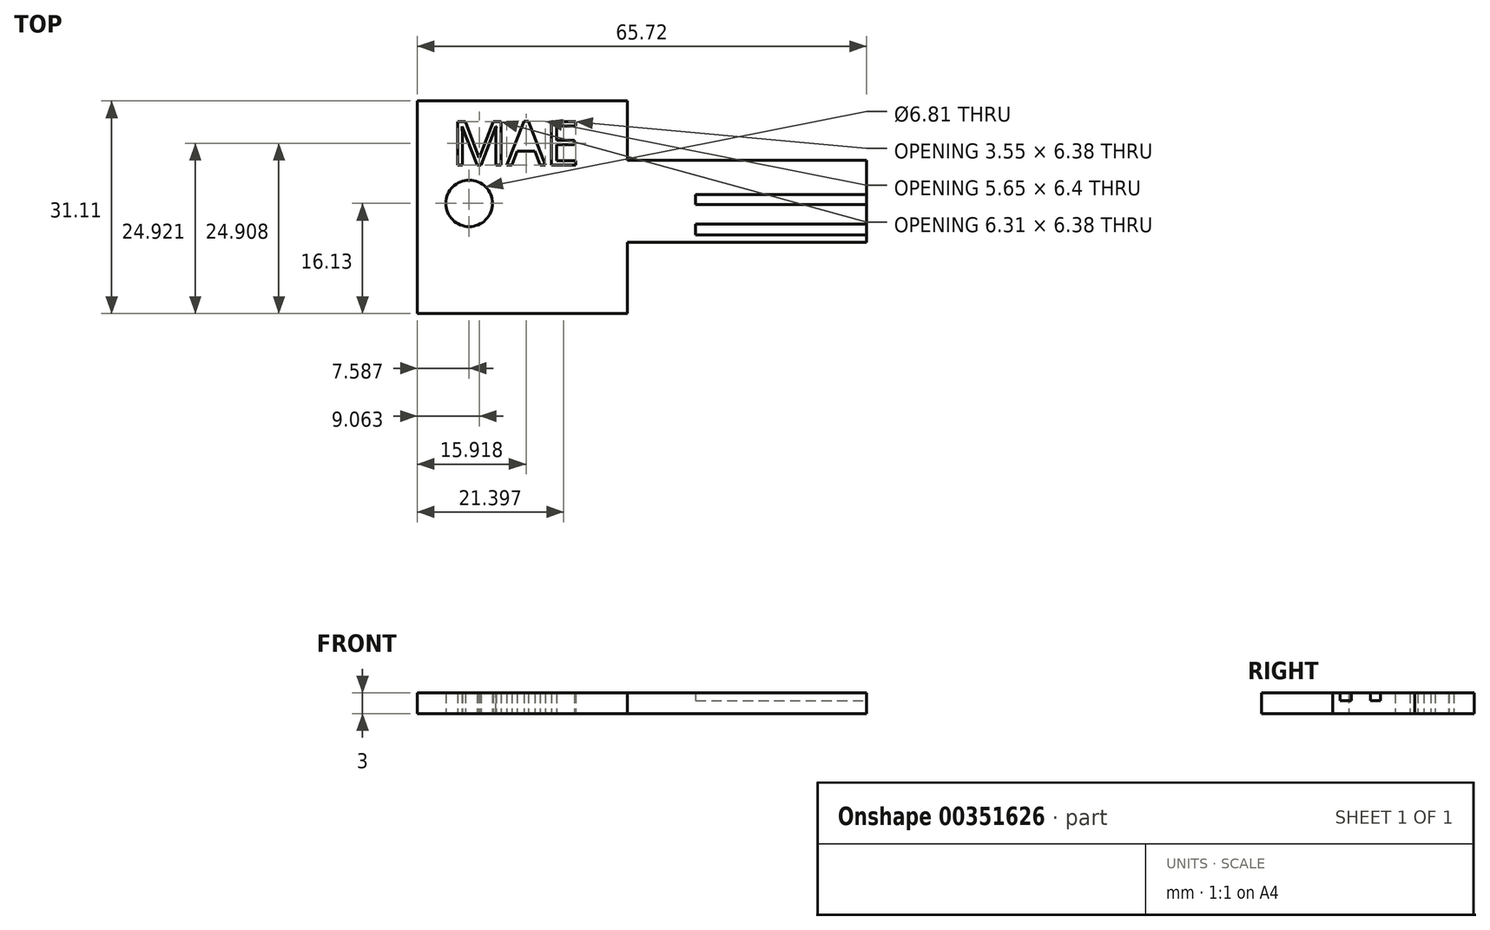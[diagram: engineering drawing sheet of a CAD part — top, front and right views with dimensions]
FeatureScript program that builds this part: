
annotation { "Feature Type Name" : "Feature", "Feature Type Description" : "" }
export const myFeature = defineFeature(function(context is Context, id is Id, definition is map)
    precondition{}
    {
        {
            var Q0;
            Q0=qCreatedBy(makeId("Top.planeOp"),FACE);
            var sketch = newSketch(context, id + "F0", { "sketchPlane" : qUnion([Q0])});
            skLineSegment(sketch, "E0.bottom", {"start": v(17.5, 6) * mm, "end": v(-17.5, 6) * mm});
            skLineSegment(sketch, "E0.top", {"start": v(17.5, -6) * mm, "end": v(-17.5, -6) * mm});
            skLineSegment(sketch, "E0.left", {"start": v(17.5, 6) * mm, "end": v(17.5, -6) * mm});
            skLineSegment(sketch, "E0.right", {"start": v(-17.5, 6) * mm, "end": v(-17.5, -6) * mm});
            skPoint(sketch, "E0.middle", {"position": v(0, 0) * mm});
            skLineSegment(sketch, "E1.bottom", {"start": v(-17.5, 14.69) * mm, "end": v(-48.22, 14.69) * mm});
            skLineSegment(sketch, "E1.top", {"start": v(-17.5, -16.42) * mm, "end": v(-48.22, -16.42) * mm});
            skLineSegment(sketch, "E1.left", {"start": v(-17.5, 14.69) * mm, "end": v(-17.5, -16.42) * mm});
            skLineSegment(sketch, "E1.right", {"start": v(-48.22, 14.69) * mm, "end": v(-48.22, -16.42) * mm});
            skCircle(sketch, "E2", {"center": v(-40.63, -0.3) * mm, "radius": 3.4 * mm});
            skPoint(sketch, "E2.first.point", {"position": v(-44.03, 0) * mm});
            skPoint(sketch, "E2.second.point", {"position": v(-38.64, -3.06) * mm});
            skPoint(sketch, "E2.third.point", {"position": v(-38.05, 1.93) * mm});
            skText(sketch, "E3", { "text": "MAE", "fontName": "OpenSans-Regular.ttf"});
            const initialGuessF0  = {"E3": [-0.04319, 0.0053, 1, 0, 0.00643]};
            skSetInitialGuess(sketch, initialGuessF0);
            skSolve(sketch);
        }
        {
            var Q0;
            {var subQ3=sQuery(id+"F0.wireOp",EDGE,"E1.bottom");Q0=makeQuery(id+"F0.imprint","IMPRINT",FACE,{"disambiguationData":[TD([[makeQuery(id+"F0.imprint","IMPRINT",EDGE,{"derivedFrom":subQ3}),1.0]])]});}
            var Q1;
            {var subQ0=sQuery(id+"F0.wireOp",EDGE,"E0.bottom");Q1=makeQuery(id+"F0.imprint","IMPRINT",FACE,{"disambiguationData":[TD([[makeQuery(id+"F0.imprint","IMPRINT",EDGE,{"derivedFrom":subQ0}),1.0]])]});}
            extrude(context, id + "F1", {"entities" : qUnion([Q0, Q1]), "depth" : 3 * mm});
        }
        {
            var Q0;
            Q0=makeQuery(id+"F1.opExtrude","SWEPT_FACE",FACE,{"disambiguationData":[OSD([sQuery(id+"F0.wireOp",EDGE,"E0.left")])]});
            var sketch = newSketch(context, id + "F2", { "sketchPlane" : qUnion([Q0])});
            skLineSegment(sketch, "E4.bottom", {"start": v(-4.92, 3) * mm, "end": v(-3.3, 3) * mm});
            skLineSegment(sketch, "E4.top", {"start": v(-4.92, 1.9) * mm, "end": v(-3.3, 1.9) * mm});
            skLineSegment(sketch, "E4.left", {"start": v(-4.92, 3) * mm, "end": v(-4.92, 1.9) * mm});
            skLineSegment(sketch, "E4.right", {"start": v(-3.3, 3) * mm, "end": v(-3.3, 1.9) * mm});
            skLineSegment(sketch, "E5.bottom", {"start": v(-0.48, 3) * mm, "end": v(1, 3) * mm});
            skLineSegment(sketch, "E5.top", {"start": v(-0.48, 1.9) * mm, "end": v(1, 1.9) * mm});
            skLineSegment(sketch, "E5.left", {"start": v(-0.48, 3) * mm, "end": v(-0.48, 1.9) * mm});
            skLineSegment(sketch, "E5.right", {"start": v(1, 3) * mm, "end": v(1, 1.9) * mm});
            skSolve(sketch);
        }
        {
            var Q0;
            Q0=makeQuery(id+"F2.imprint","IMPRINT",FACE,{"disambiguationData":[TD([[makeQuery(id+"F2.imprint","IMPRINT",EDGE,{"derivedFrom":sQuery(id+"F2.wireOp",EDGE,"E4.bottom")}),1.0]])]});
            var Q1;
            Q1=makeQuery(id+"F2.imprint","IMPRINT",FACE,{"disambiguationData":[TD([[makeQuery(id+"F2.imprint","IMPRINT",EDGE,{"derivedFrom":sQuery(id+"F2.wireOp",EDGE,"E5.bottom")}),1.0]])]});
            extrude(context, id + "F3", {"entities" : qUnion([Q0, Q1]), "operationType" : NewBodyOperationType.REMOVE, "oppositeDirection" : true, "depth" : 25 * mm});
        }
    });
